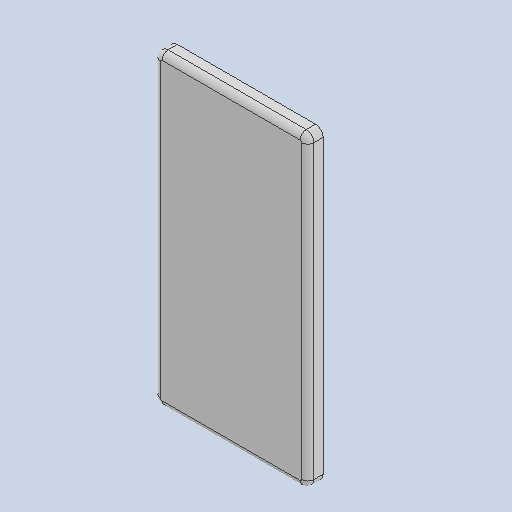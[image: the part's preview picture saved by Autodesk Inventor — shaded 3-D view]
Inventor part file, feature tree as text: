
AUTODESK INVENTOR PART (.ipt)
format: ipt  version: 2022 (Build 260153000, 153)  size: 94,208 bytes
history: native  units: in
note: dims shown in document units (in); Inventor stores cm internally (conversion verified against a paired STEP export)
features: fillet x1
ambient origin geometry x8: Origin, YZ Plane, XZ Plane, XY Plane, X Axis, Y Axis, Z Axis, Center Point
bodies: Solid1 (feature_tree)
feature tree (1):
  fillet  "Fillet1"  [1 undecoded]
note: 1 required parameter value undecoded (feature->parameter linkage not recoverable at this tier; creation-order binding heuristic only, values carry confidence <= 0.55)
